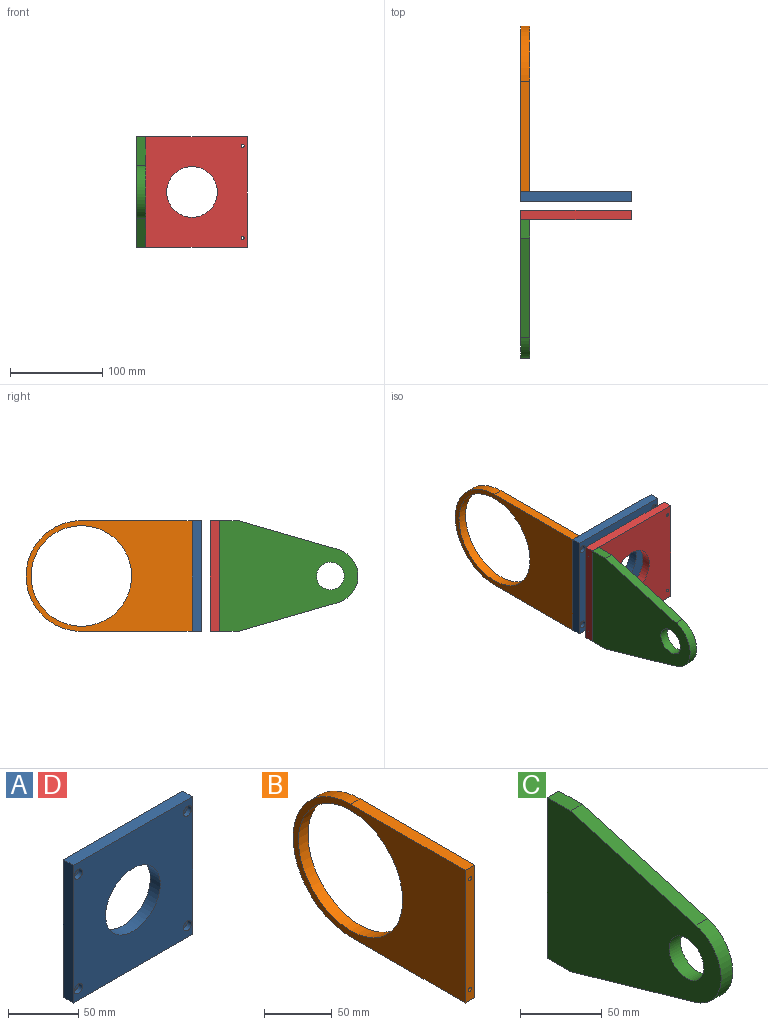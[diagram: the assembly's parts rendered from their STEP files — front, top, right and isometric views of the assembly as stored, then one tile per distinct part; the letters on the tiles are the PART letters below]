
ASSEMBLY  parts=4 mates=3
PART A: 19 faces, bbox 120x10x120 mm
  f0: plane 120x10mm, normal (0,0,1), area 1200mm2, adj f1,f3,f4,f5
  f1: plane 120x10mm, normal (-1,0,0), area 1200mm2, adj f0,f2,f4,f5
  f2: plane 120x10mm, normal (0,0,-1), area 1200mm2, adj f1,f3,f4,f5
  f3: plane 120x10mm, normal (1,0,0), area 1200mm2, adj f0,f2,f4,f5
  f4: plane 120x120mm, normal (0,-1,0), area 11810.3mm2, adj f0,f1,f2,f3,f6,f9,f12,f15
  f5: plane 120x120mm, normal (0,1,0), area 11990mm2, adj f0,f1,f2,f3,f6,f7,f10,f13
  f6: cylinder r=27.5mm len=55mm, axis (0,1,0), area 1727.9mm2, adj f4,f5
  f7: cylinder r=1.65mm len=6mm, axis (0,-1,0), area 62.2mm2, adj f5,f8
  f8: plane 8.25x8.25mm, normal (0,-1,0), area 44.9mm2, adj f7,f9
  f9: cylinder r=4.12mm len=8.25mm, axis (0,-1,0), area 103.7mm2, adj f4,f8
  f10: cylinder r=1.65mm len=6mm, axis (0,-1,0), area 62.2mm2, adj f5,f11
  f11: plane 8.25x8.25mm, normal (0,-1,0), area 44.9mm2, adj f10,f12
  f12: cylinder r=4.12mm len=8.25mm, axis (0,-1,0), area 103.7mm2, adj f4,f11
  f13: cylinder r=1.65mm len=6mm, axis (0,-1,0), area 62.2mm2, adj f5,f14
  f14: plane 8.25x8.25mm, normal (0,-1,0), area 44.9mm2, adj f13,f15
  f15: cylinder r=4.12mm len=8.25mm, axis (0,-1,0), area 103.7mm2, adj f4,f14
  f16: cylinder r=1.65mm len=6mm, axis (0,-1,0), area 62.2mm2, adj f5,f17
  f17: plane 8.25x8.25mm, normal (0,-1,0), area 44.9mm2, adj f16,f18
  f18: cylinder r=4.12mm len=8.25mm, axis (0,-1,0), area 103.7mm2, adj f4,f17
PART B: 11 faces, bbox 10x180x120 mm
  f0: cylinder r=60mm len=120mm, axis (-1,0,0), area 1885mm2, adj f1,f3,f5,f6
  f1: plane 120x10mm, normal (0,0,1), area 1200mm2, adj f0,f2,f5,f6
  f2: plane 120x10mm, normal (0,-1,0), area 1182.9mm2, adj f1,f3,f5,f6,f8,f10
  f3: plane 120x10mm, normal (0,0,-1), area 1200mm2, adj f0,f2,f5,f6
  f4: cylinder r=54.5mm len=109mm, axis (-1,0,0), area 3424.3mm2, adj f5,f6
  f5: plane 180x120mm, normal (1,0,0), area 10723.6mm2, adj f0,f1,f2,f3,f4
  f6: plane 180x120mm, normal (-1,0,0), area 10723.6mm2, adj f0,f1,f2,f3,f4
  f7: cone r=0mm half-angle=59deg, axis (0,-1,0), area 10mm2, adj f8
  f8: cylinder r=1.65mm len=13.5mm, axis (0,-1,0), area 140mm2, adj f2,f7
  f9: cone r=0mm half-angle=59deg, axis (0,-1,0), area 10mm2, adj f10
  f10: cylinder r=1.65mm len=13.5mm, axis (0,-1,0), area 140mm2, adj f2,f9
PART C: 13 faces, bbox 10x150x120 mm
  f0: plane 20x10mm, normal (0,0,-1), area 200mm2, adj f1,f6,f7,f8
  f1: plane 120x10mm, normal (0,1,0), area 1182.9mm2, adj f0,f2,f7,f8,f10,f12
  f2: plane 20x10mm, normal (0,0,1), area 200mm2, adj f1,f3,f7,f8
  f3: plane 108.3x31.17mm, normal (0,-0.28,0.96), area 1126.9mm2, adj f2,f4,f7,f8
  f4: cylinder r=30mm len=57.66mm, axis (-1,0,0), area 774.3mm2, adj f3,f6,f7,f8
  f5: cylinder r=15mm len=30mm, axis (-1,0,0), area 942.5mm2, adj f7,f8
  f6: plane 108.3x31.17mm, normal (0,-0.28,-0.96), area 1126.9mm2, adj f0,f4,f7,f8
  f7: plane 150x120mm, normal (1,0,0), area 12235.5mm2, adj f0,f1,f2,f3,f4,f5,f6
  f8: plane 150x120mm, normal (-1,0,0), area 12235.5mm2, adj f0,f1,f2,f3,f4,f5,f6
  f9: cone r=0mm half-angle=59deg, axis (0,1,0), area 10mm2, adj f10
  f10: cylinder r=1.65mm len=13.5mm, axis (0,1,0), area 140mm2, adj f1,f9
  f11: cone r=0mm half-angle=59deg, axis (0,1,0), area 10mm2, adj f12
  f12: cylinder r=1.65mm len=13.5mm, axis (0,1,0), area 140mm2, adj f1,f11
PART D: same geometry as A
PLACE A rot(axis=(0,1,0),0deg) t=(50,-120,0)mm
PLACE B rot(axis=(0,1,0),0deg) t=(-10,0,0)mm
PLACE C rot(axis=(0.54,0.83,0.11),0deg) t=(-10,-30,0)mm
PLACE D rot(axis=(0,0,-1),180deg) t=(50,-150,0)mm
MATE fastened C.f9 <-> D.f7  axis (0,1,0) through (-5,-150,50)mm
MATE fastened D.f6 <-> A.f6  axis (0,-1,0) through (50,-140,0)mm
MATE fastened A.f10 <-> B.f7  axis (0,1,0) through (-5,-120,50)mm
